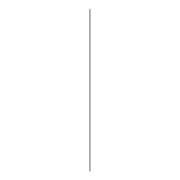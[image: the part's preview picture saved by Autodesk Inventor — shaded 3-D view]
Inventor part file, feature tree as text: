
AUTODESK INVENTOR PART (.ipt)
format: ipt  version: 2022 (Build 260153000, 153)  size: 73,728 bytes
history: native  units: mm
features: extrude x1, sketch x1
ambient origin geometry x8: Origin, YZ Plane, XZ Plane, XY Plane, X Axis, Y Axis, Z Axis, Center Point
bodies: Solid1 (feature_tree)
feature tree (2):
  extrude  "Extrusion1"  Depth=500.0mm TaperAngle=0.0deg
  sketch  "Sketch1"  dims[d0=4.0mm d1=500.0mm d2=0.0mm]
